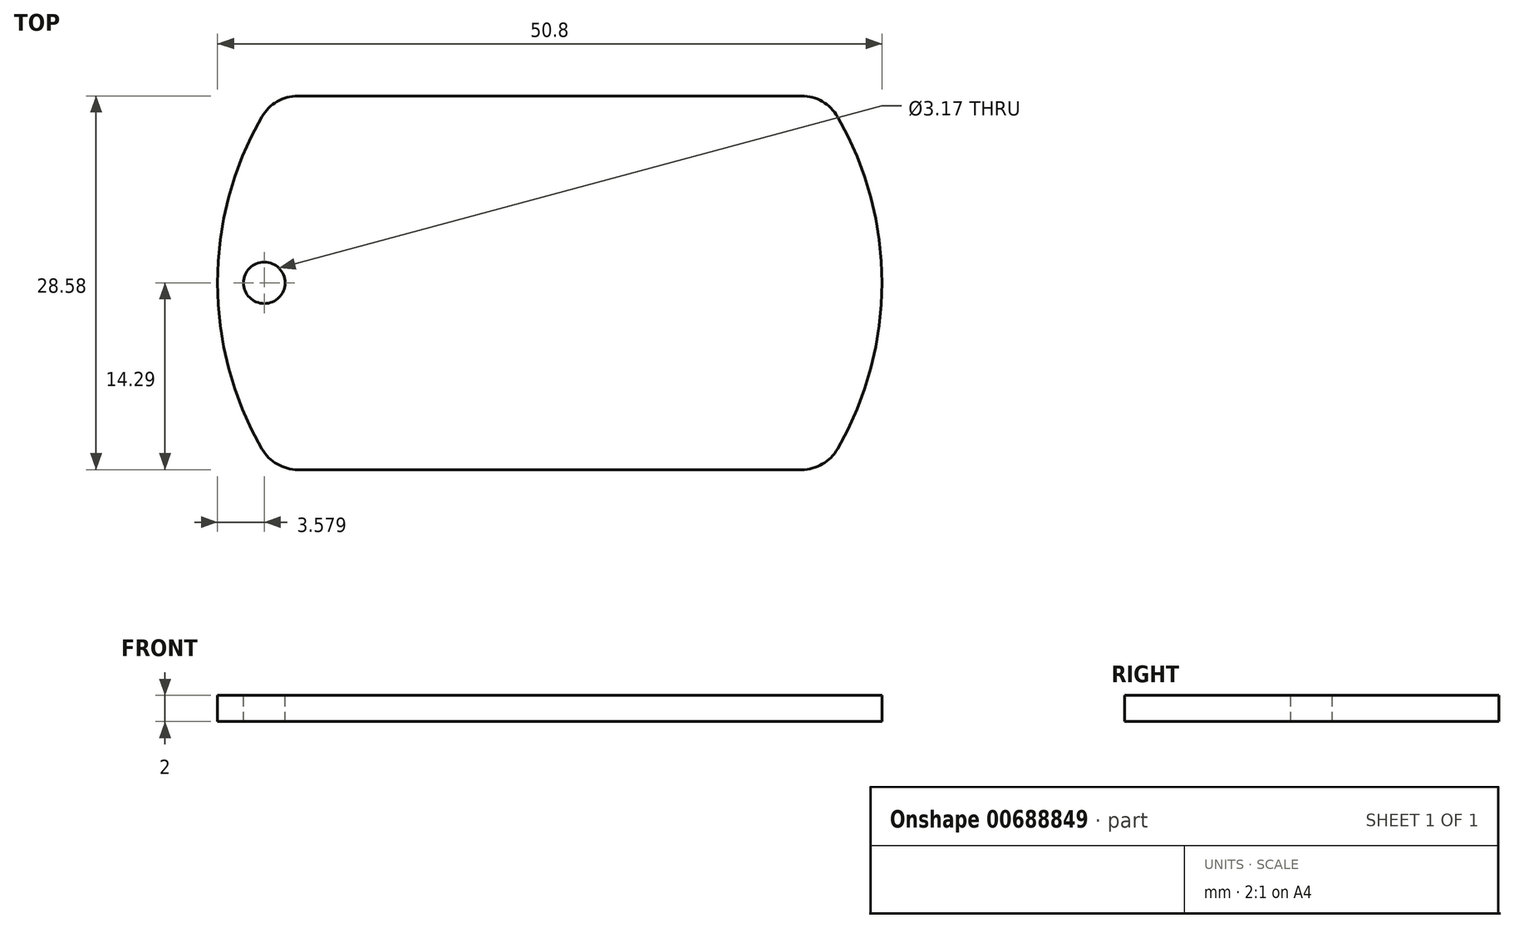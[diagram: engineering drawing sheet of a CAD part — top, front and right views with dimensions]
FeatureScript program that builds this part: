
annotation { "Feature Type Name" : "Feature", "Feature Type Description" : "" }
export const myFeature = defineFeature(function(context is Context, id is Id, definition is map)
    precondition{}
    {
        {
            var Q0;
            Q0=qCreatedBy(makeId("Top.planeOp"),FACE);
            var sketch = newSketch(context, id + "F0", { "sketchPlane" : qUnion([Q0])});
            skArc(sketch, "E0", {"start": v(-22, 12.7) * mm, "mid": v(-25.4, 0) * mm, "end": v(-22, -12.7) * mm});
            skLineSegment(sketch, "E1.top", {"start": v(-19.25, -14.29) * mm, "end": v(19.25, -14.29) * mm});
            skArc(sketch, "E2.trimOffspring", {"start": v(22, -12.7) * mm, "mid": v(25.4, 0) * mm, "end": v(22, 12.7) * mm});
            skLineSegment(sketch, "E3", {"start": v(-19.25, 14.29) * mm, "end": v(19.25, 14.29) * mm});
            skPoint(sketch, "E4.visualSharp", {"position": v(-21, 14.29) * mm});
            skArc(sketch, "E4.filletArc", {"start": v(-19.25, 14.29) * mm, "mid": v(-20.83, 13.86) * mm, "end": v(-22, 12.7) * mm});
            skPoint(sketch, "E5.visualSharp", {"position": v(21, 14.29) * mm});
            skArc(sketch, "E5.filletArc", {"start": v(22, 12.7) * mm, "mid": v(20.83, 13.86) * mm, "end": v(19.25, 14.29) * mm});
            skPoint(sketch, "E6.visualSharp", {"position": v(21, -14.29) * mm});
            skArc(sketch, "E6.filletArc", {"start": v(19.25, -14.29) * mm, "mid": v(20.83, -13.86) * mm, "end": v(22, -12.7) * mm});
            skPoint(sketch, "E7.visualSharp", {"position": v(-21, -14.29) * mm});
            skArc(sketch, "E7.filletArc", {"start": v(-22, -12.7) * mm, "mid": v(-20.83, -13.86) * mm, "end": v(-19.25, -14.29) * mm});
            skSolve(sketch);
        }
        {
            var Q0;
            Q0=makeQuery(id+"F0.imprint","IMPRINT",FACE,{"disambiguationData":[TD([[makeQuery(id+"F0.imprint","IMPRINT",EDGE,{"derivedFrom":sQuery(id+"F0.wireOp",EDGE,"E0")}),1.0]])]});
            extrude(context, id + "F1", {"entities" : qUnion([Q0]), "depth" : 1 * mm, "offsetDistance" : 25.4 * mm});
        }
        {
            var Q0;
            Q0=makeQuery(id+"F1.opExtrude","CAP_FACE",FACE,{"disambiguationData":[OSD([sQuery(id+"F0.wireOp",EDGE,"E0"),sQuery(id+"F0.wireOp",EDGE,"E1.top"),sQuery(id+"F0.wireOp",EDGE,"E2.trimOffspring"),sQuery(id+"F0.wireOp",EDGE,"E3"),sQuery(id+"F0.wireOp",EDGE,"E4.filletArc"),sQuery(id+"F0.wireOp",EDGE,"E5.filletArc"),sQuery(id+"F0.wireOp",EDGE,"E6.filletArc"),sQuery(id+"F0.wireOp",EDGE,"E7.filletArc")])],"isStart":false});
            var sketch = newSketch(context, id + "F2", { "sketchPlane" : qUnion([Q0])});
            skLineSegment(sketch, "E8.0", {"start": v(-18.66, 13.29) * mm, "end": v(18.66, 13.29) * mm});
            skArc(sketch, "E8.1", {"start": v(-21.45, 11.63) * mm, "mid": v(-24.4, 0) * mm, "end": v(-21.45, -11.63) * mm});
            skLineSegment(sketch, "E8.2", {"start": v(-18.66, -13.29) * mm, "end": v(18.66, -13.29) * mm});
            skArc(sketch, "E8.3", {"start": v(21.45, -11.63) * mm, "mid": v(24.4, 0) * mm, "end": v(21.45, 11.63) * mm});
            skPoint(sketch, "E9.visualSharp", {"position": v(-20.46, 13.29) * mm});
            skArc(sketch, "E9.filletArc", {"start": v(-18.66, 13.29) * mm, "mid": v(-20.29, 12.84) * mm, "end": v(-21.45, 11.63) * mm});
            skPoint(sketch, "E10.visualSharp", {"position": v(20.46, 13.29) * mm});
            skArc(sketch, "E10.filletArc", {"start": v(21.45, 11.63) * mm, "mid": v(20.29, 12.84) * mm, "end": v(18.66, 13.29) * mm});
            skPoint(sketch, "E11.visualSharp", {"position": v(20.46, -13.29) * mm});
            skArc(sketch, "E11.filletArc", {"start": v(18.66, -13.29) * mm, "mid": v(20.29, -12.84) * mm, "end": v(21.45, -11.63) * mm});
            skPoint(sketch, "E12.visualSharp", {"position": v(-20.46, -13.29) * mm});
            skArc(sketch, "E12.filletArc", {"start": v(-21.45, -11.63) * mm, "mid": v(-20.29, -12.84) * mm, "end": v(-18.66, -13.29) * mm});
            skLineSegment(sketch, "E13.0", {"start": v(-19.25, 14.29) * mm, "end": v(19.25, 14.29) * mm});
            skArc(sketch, "E13.1", {"start": v(-22, 12.7) * mm, "mid": v(-25.4, 0) * mm, "end": v(-22, -12.7) * mm});
            skLineSegment(sketch, "E13.2", {"start": v(-19.25, -14.29) * mm, "end": v(19.25, -14.29) * mm});
            skArc(sketch, "E13.3", {"start": v(22, -12.7) * mm, "mid": v(25.4, 0) * mm, "end": v(22, 12.7) * mm});
            skPoint(sketch, "E14.visualSharp", {"position": v(-21, -14.29) * mm});
            skArc(sketch, "E14.filletArc", {"start": v(-22, -12.7) * mm, "mid": v(-20.83, -13.86) * mm, "end": v(-19.25, -14.29) * mm});
            skPoint(sketch, "E15.visualSharp", {"position": v(21, -14.29) * mm});
            skArc(sketch, "E15.filletArc", {"start": v(19.25, -14.29) * mm, "mid": v(20.83, -13.86) * mm, "end": v(22, -12.7) * mm});
            skPoint(sketch, "E16.visualSharp", {"position": v(21, 14.29) * mm});
            skArc(sketch, "E16.filletArc", {"start": v(22, 12.7) * mm, "mid": v(20.83, 13.86) * mm, "end": v(19.25, 14.29) * mm});
            skPoint(sketch, "E17.visualSharp", {"position": v(-21, 14.29) * mm});
            skArc(sketch, "E17.filletArc", {"start": v(-19.25, 14.29) * mm, "mid": v(-20.83, 13.86) * mm, "end": v(-22, 12.7) * mm});
            skSolve(sketch);
        }
        {
            var Q0;
            Q0=makeQuery(id+"F2.imprint","IMPRINT",FACE,{"disambiguationData":[TD([[makeQuery(id+"F2.imprint","IMPRINT",EDGE,{"derivedFrom":sQuery(id+"F2.wireOp",EDGE,"E8.0")}),1.0]])]});
            extrude(context, id + "F3", {"entities" : qUnion([Q0]), "operationType" : NewBodyOperationType.ADD, "depth" : 1 * mm, "offsetDistance" : 25.4 * mm});
        }
        {
            var Q0;
            Q0=makeQuery(id+"F1.opExtrude","CAP_FACE",FACE,{"disambiguationData":[OSD([sQuery(id+"F0.wireOp",EDGE,"E0"),sQuery(id+"F0.wireOp",EDGE,"E1.top"),sQuery(id+"F0.wireOp",EDGE,"E2.trimOffspring"),sQuery(id+"F0.wireOp",EDGE,"E3"),sQuery(id+"F0.wireOp",EDGE,"E4.filletArc"),sQuery(id+"F0.wireOp",EDGE,"E5.filletArc"),sQuery(id+"F0.wireOp",EDGE,"E6.filletArc"),sQuery(id+"F0.wireOp",EDGE,"E7.filletArc")])],"isStart":false});
            var sketch = newSketch(context, id + "F4", { "sketchPlane" : qUnion([Q0])});
            skCircle(sketch, "E18", {"center": v(-21.82, 0) * mm, "radius": 1.59 * mm});
            skSolve(sketch);
        }
        {
            var Q0;
            Q0=makeQuery(id+"F4.imprint","IMPRINT",FACE,{"disambiguationData":[TD([[makeQuery(id+"F4.imprint","IMPRINT",EDGE,{"derivedFrom":sQuery(id+"F4.wireOp",EDGE,"E18")}),1.0]])]});
            extrude(context, id + "F5", {"entities" : qUnion([Q0]), "operationType" : NewBodyOperationType.REMOVE, "oppositeDirection" : true, "depth" : 1 * mm, "offsetDistance" : 25.4 * mm});
        }
        {
            var Q0;
            Q0=makeQuery(id+"F1.opExtrude","CAP_FACE",FACE,{"disambiguationData":[OSD([sQuery(id+"F0.wireOp",EDGE,"E0"),sQuery(id+"F0.wireOp",EDGE,"E1.top"),sQuery(id+"F0.wireOp",EDGE,"E2.trimOffspring"),sQuery(id+"F0.wireOp",EDGE,"E3"),sQuery(id+"F0.wireOp",EDGE,"E4.filletArc"),sQuery(id+"F0.wireOp",EDGE,"E5.filletArc"),sQuery(id+"F0.wireOp",EDGE,"E6.filletArc"),sQuery(id+"F0.wireOp",EDGE,"E7.filletArc")])],"isStart":false});
            var sketch = newSketch(context, id + "F6", { "sketchPlane" : qUnion([Q0])});
            skText(sketch, "E19", { "text": "Zak", "fontName": "OpenSans-Regular.ttf"});
            const initialGuessF6  = {"E19": [-0.0169, -0.00676, 1, 0, 0.01427]};
            skSetInitialGuess(sketch, initialGuessF6);
            skSolve(sketch);
        }
        {
            var Q0;
            Q0 = qSketchRegion(id + "F6", true);
            extrude(context, id + "F7", {"entities" : qUnion([Q0]), "operationType" : NewBodyOperationType.ADD, "depth" : 1 * mm, "offsetDistance" : 25.4 * mm});
        }
        {
            var Q0;
            Q0=makeQuery(id+"F1.opExtrude","CAP_FACE",FACE,{"disambiguationData":[OSD([sQuery(id+"F0.wireOp",EDGE,"E0"),sQuery(id+"F0.wireOp",EDGE,"E1.top"),sQuery(id+"F0.wireOp",EDGE,"E2.trimOffspring"),sQuery(id+"F0.wireOp",EDGE,"E3"),sQuery(id+"F0.wireOp",EDGE,"E4.filletArc"),sQuery(id+"F0.wireOp",EDGE,"E5.filletArc"),sQuery(id+"F0.wireOp",EDGE,"E6.filletArc"),sQuery(id+"F0.wireOp",EDGE,"E7.filletArc")])],"isStart":false});
            var Q1;
            Q1 = qSketchRegion(id + "F6", true);
            extrude(context, id + "F8", {"entities" : qUnion([Q0, Q1]), "operationType" : NewBodyOperationType.ADD, "depth" : 1 * mm, "offsetDistance" : 25.4 * mm});
        }
    });
